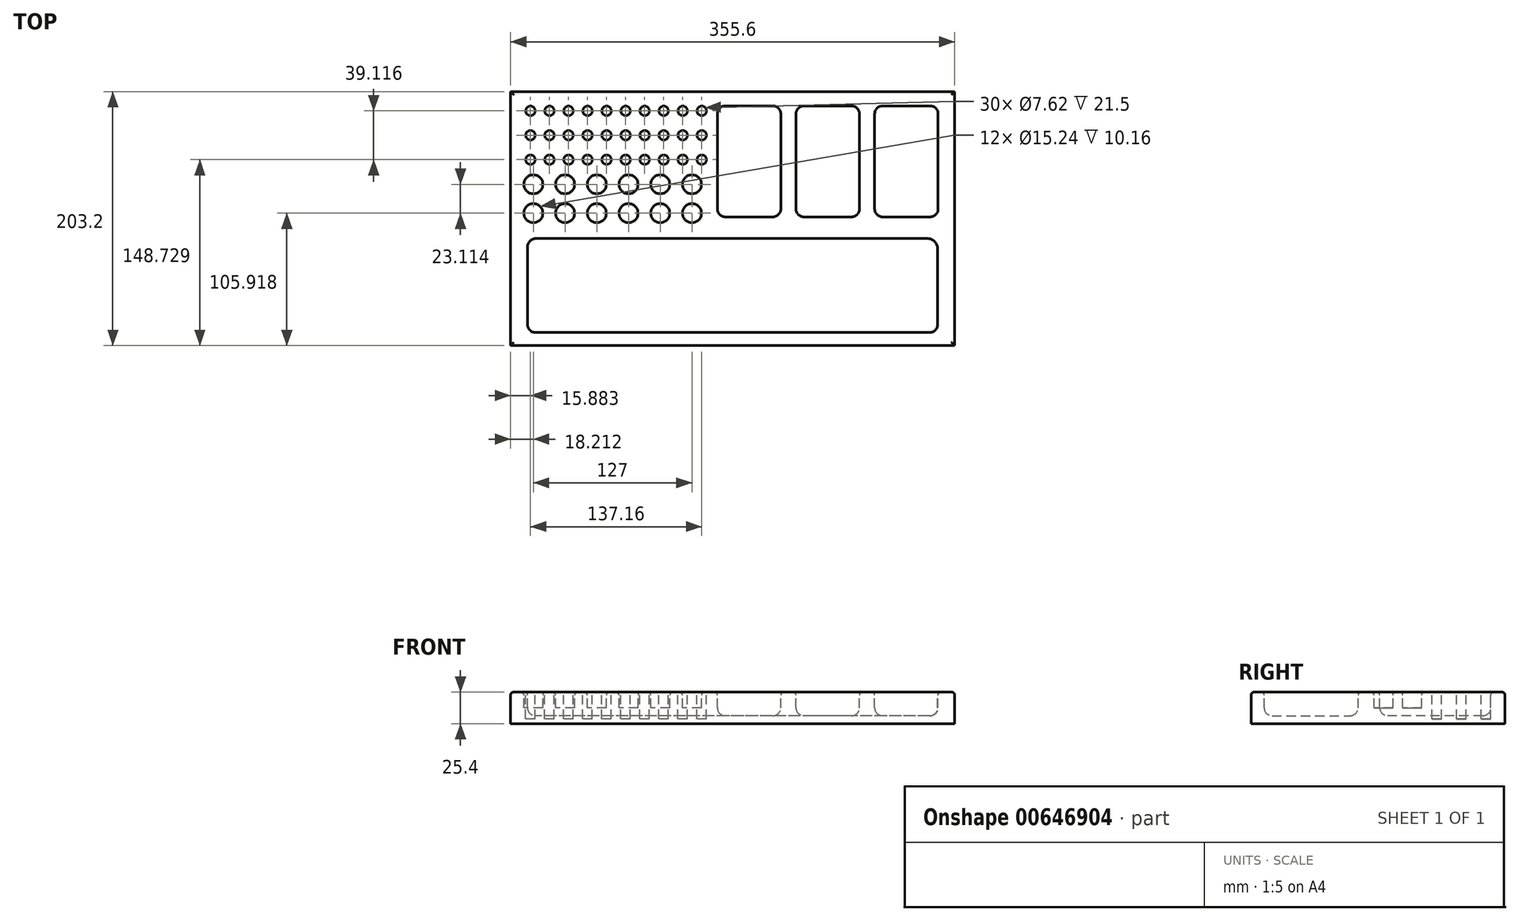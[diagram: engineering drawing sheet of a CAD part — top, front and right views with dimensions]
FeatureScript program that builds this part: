
annotation { "Feature Type Name" : "Feature", "Feature Type Description" : "" }
export const myFeature = defineFeature(function(context is Context, id is Id, definition is map)
    precondition{}
    {
        {
            var Q0;
            Q0=qCreatedBy(makeId("Top.planeOp"),FACE);
            var sketch = newSketch(context, id + "F0", { "sketchPlane" : qUnion([Q0])});
            skLineSegment(sketch, "E0.bottom", {"start": v(-59.89, 153) * mm, "end": v(295.71, 153) * mm});
            skLineSegment(sketch, "E0.top", {"start": v(-59.89, -50.2) * mm, "end": v(295.71, -50.2) * mm});
            skLineSegment(sketch, "E0.left", {"start": v(-59.89, 153) * mm, "end": v(-59.89, -50.2) * mm});
            skLineSegment(sketch, "E0.right", {"start": v(295.71, 153) * mm, "end": v(295.71, -50.2) * mm});
            skLineSegment(sketch, "E1", {"start": v(295.71, -6.07) * mm, "end": v(295.71, 49.4) * mm});
            skLineSegment(sketch, "E2.bottom", {"start": v(275.71, -39.83) * mm, "end": v(-39.97, -39.83) * mm});
            skLineSegment(sketch, "E2.top", {"start": v(273.64, 35.42) * mm, "end": v(-39.64, 35.42) * mm});
            skLineSegment(sketch, "E2.left", {"start": v(282.06, -33.48) * mm, "end": v(282.06, 27) * mm});
            skLineSegment(sketch, "E2.right", {"start": v(-46.32, -33.48) * mm, "end": v(-46.32, 28.74) * mm});
            skPoint(sketch, "E2.middle", {"position": v(117.87, -2.2) * mm});
            skCircle(sketch, "E3", {"center": v(-41.68, 78.82) * mm, "radius": 7.62 * mm});
            skCircle(sketch, "E4.0.1.0", {"center": v(-41.68, 55.7) * mm, "radius": 7.62 * mm});
            skCircle(sketch, "E4.1.0.0", {"center": v(-16.28, 78.82) * mm, "radius": 7.62 * mm});
            skCircle(sketch, "E4.1.1.0", {"center": v(-16.28, 55.7) * mm, "radius": 7.62 * mm});
            skCircle(sketch, "E4.2.0.0", {"center": v(9.12, 78.82) * mm, "radius": 7.62 * mm});
            skCircle(sketch, "E4.2.1.0", {"center": v(9.12, 55.7) * mm, "radius": 7.62 * mm});
            skCircle(sketch, "E4.3.0.0", {"center": v(34.52, 78.82) * mm, "radius": 7.62 * mm});
            skCircle(sketch, "E4.3.1.0", {"center": v(34.52, 55.7) * mm, "radius": 7.62 * mm});
            skLineSegment(sketch, "E4.direction1", {"start": v(-41.68, 78.82) * mm, "end": v(-16.28, 78.82) * mm, "construction": true});
            skLineSegment(sketch, "E4.direction2", {"start": v(-41.68, 78.82) * mm, "end": v(-41.68, 55.7) * mm, "construction": true});
            skCircle(sketch, "E5", {"center": v(-44, 137.63) * mm, "radius": 3.81 * mm});
            skCircle(sketch, "E6.0.1.0", {"center": v(-44, 118.08) * mm, "radius": 3.81 * mm});
            skCircle(sketch, "E6.0.2.0", {"center": v(-44, 98.52) * mm, "radius": 3.81 * mm});
            skCircle(sketch, "E6.1.0.0", {"center": v(-28.77, 137.63) * mm, "radius": 3.81 * mm});
            skCircle(sketch, "E6.1.1.0", {"center": v(-28.77, 118.08) * mm, "radius": 3.81 * mm});
            skCircle(sketch, "E6.1.2.0", {"center": v(-28.77, 98.52) * mm, "radius": 3.81 * mm});
            skCircle(sketch, "E6.2.0.0", {"center": v(-13.53, 137.63) * mm, "radius": 3.81 * mm});
            skCircle(sketch, "E6.2.1.0", {"center": v(-13.53, 118.08) * mm, "radius": 3.81 * mm});
            skCircle(sketch, "E6.2.2.0", {"center": v(-13.53, 98.52) * mm, "radius": 3.81 * mm});
            skCircle(sketch, "E6.3.0.0", {"center": v(1.71, 137.63) * mm, "radius": 3.81 * mm});
            skCircle(sketch, "E6.3.1.0", {"center": v(1.71, 118.08) * mm, "radius": 3.81 * mm});
            skCircle(sketch, "E6.3.2.0", {"center": v(1.71, 98.52) * mm, "radius": 3.81 * mm});
            skCircle(sketch, "E6.4.0.0", {"center": v(16.95, 137.63) * mm, "radius": 3.81 * mm});
            skCircle(sketch, "E6.4.1.0", {"center": v(16.95, 118.08) * mm, "radius": 3.81 * mm});
            skCircle(sketch, "E6.4.2.0", {"center": v(16.95, 98.52) * mm, "radius": 3.81 * mm});
            skCircle(sketch, "E6.5.0.0", {"center": v(32.2, 137.63) * mm, "radius": 3.81 * mm});
            skCircle(sketch, "E6.5.1.0", {"center": v(32.2, 118.08) * mm, "radius": 3.81 * mm});
            skCircle(sketch, "E6.5.2.0", {"center": v(32.2, 98.52) * mm, "radius": 3.81 * mm});
            skCircle(sketch, "E6.6.0.0", {"center": v(47.43, 137.63) * mm, "radius": 3.81 * mm});
            skCircle(sketch, "E6.6.1.0", {"center": v(47.43, 118.08) * mm, "radius": 3.81 * mm});
            skCircle(sketch, "E6.6.2.0", {"center": v(47.43, 98.52) * mm, "radius": 3.81 * mm});
            skCircle(sketch, "E6.7.0.0", {"center": v(62.67, 137.63) * mm, "radius": 3.81 * mm});
            skCircle(sketch, "E6.7.1.0", {"center": v(62.67, 118.08) * mm, "radius": 3.81 * mm});
            skCircle(sketch, "E6.7.2.0", {"center": v(62.67, 98.52) * mm, "radius": 3.81 * mm});
            skLineSegment(sketch, "E6.direction1", {"start": v(-44, 137.63) * mm, "end": v(-28.77, 137.63) * mm, "construction": true});
            skLineSegment(sketch, "E6.direction2", {"start": v(-44, 137.63) * mm, "end": v(-44, 118.08) * mm, "construction": true});
            skPoint(sketch, "E7.visualSharp", {"position": v(282.06, 35.42) * mm});
            skArc(sketch, "E7.filletArc", {"start": v(282.06, 27) * mm, "mid": v(279.6, 32.95) * mm, "end": v(273.64, 35.42) * mm});
            skPoint(sketch, "E8.visualSharp", {"position": v(282.06, -39.83) * mm});
            skArc(sketch, "E8.filletArc", {"start": v(275.71, -39.83) * mm, "mid": v(280.2, -37.97) * mm, "end": v(282.06, -33.48) * mm});
            skPoint(sketch, "E9.visualSharp", {"position": v(-46.32, -39.83) * mm});
            skArc(sketch, "E9.filletArc", {"start": v(-46.32, -33.48) * mm, "mid": v(-44.46, -37.97) * mm, "end": v(-39.97, -39.83) * mm});
            skPoint(sketch, "E10.visualSharp", {"position": v(-46.32, 35.42) * mm});
            skArc(sketch, "E10.filletArc", {"start": v(-39.64, 35.42) * mm, "mid": v(-44.36, 33.47) * mm, "end": v(-46.32, 28.74) * mm});
            skLineSegment(sketch, "E11.bottom", {"start": v(150.11, 141.61) * mm, "end": v(112.01, 141.61) * mm});
            skLineSegment(sketch, "E11.top", {"start": v(150.11, 52.71) * mm, "end": v(112.01, 52.71) * mm});
            skLineSegment(sketch, "E11.left", {"start": v(156.46, 135.26) * mm, "end": v(156.46, 59.06) * mm});
            skLineSegment(sketch, "E11.right", {"start": v(105.66, 135.26) * mm, "end": v(105.66, 59.06) * mm});
            skPoint(sketch, "E11.middle", {"position": v(131.06, 97.16) * mm});
            skPoint(sketch, "E12.visualSharp", {"position": v(105.66, 141.61) * mm});
            skArc(sketch, "E12.filletArc", {"start": v(112.01, 141.61) * mm, "mid": v(107.52, 139.75) * mm, "end": v(105.66, 135.26) * mm});
            skPoint(sketch, "E13.visualSharp", {"position": v(156.46, 141.61) * mm});
            skArc(sketch, "E13.filletArc", {"start": v(156.46, 135.26) * mm, "mid": v(154.6, 139.75) * mm, "end": v(150.11, 141.61) * mm});
            skPoint(sketch, "E14.visualSharp", {"position": v(156.46, 52.71) * mm});
            skArc(sketch, "E14.filletArc", {"start": v(150.11, 52.71) * mm, "mid": v(154.6, 54.57) * mm, "end": v(156.46, 59.06) * mm});
            skPoint(sketch, "E15.visualSharp", {"position": v(105.66, 52.71) * mm});
            skArc(sketch, "E15.filletArc", {"start": v(105.66, 59.06) * mm, "mid": v(107.52, 54.57) * mm, "end": v(112.01, 52.71) * mm});
            skPoint(sketch, "E16.1.0.0", {"position": v(194.05, 97.16) * mm});
            skPoint(sketch, "E16.1.0.1", {"position": v(219.45, 52.71) * mm});
            skPoint(sketch, "E16.1.0.2", {"position": v(168.65, 52.71) * mm});
            skLineSegment(sketch, "E16.1.0.3", {"start": v(219.45, 135.26) * mm, "end": v(219.45, 59.06) * mm});
            skLineSegment(sketch, "E16.1.0.4", {"start": v(213.1, 141.61) * mm, "end": v(175, 141.61) * mm});
            skPoint(sketch, "E16.1.0.5", {"position": v(219.45, 141.61) * mm});
            skLineSegment(sketch, "E16.1.0.6", {"start": v(213.1, 52.71) * mm, "end": v(175, 52.71) * mm});
            skPoint(sketch, "E16.1.0.7", {"position": v(168.65, 141.61) * mm});
            skLineSegment(sketch, "E16.1.0.8", {"start": v(168.65, 135.26) * mm, "end": v(168.65, 59.06) * mm});
            skArc(sketch, "E16.1.0.9", {"start": v(175, 141.61) * mm, "mid": v(170.51, 139.75) * mm, "end": v(168.65, 135.26) * mm});
            skArc(sketch, "E16.1.0.10", {"start": v(168.65, 59.06) * mm, "mid": v(170.51, 54.57) * mm, "end": v(175, 52.71) * mm});
            skArc(sketch, "E16.1.0.11", {"start": v(213.1, 52.71) * mm, "mid": v(217.6, 54.57) * mm, "end": v(219.45, 59.06) * mm});
            skArc(sketch, "E16.1.0.12", {"start": v(219.45, 135.26) * mm, "mid": v(217.6, 139.75) * mm, "end": v(213.1, 141.61) * mm});
            skLineSegment(sketch, "E16.direction1", {"start": v(131.06, 97.16) * mm, "end": v(194.05, 97.16) * mm, "construction": true});
            skPoint(sketch, "E17.0.2.0", {"position": v(257.04, 97.16) * mm});
            skPoint(sketch, "E17.1.2.0", {"position": v(282.44, 52.71) * mm});
            skPoint(sketch, "E17.2.2.0", {"position": v(231.64, 52.71) * mm});
            skLineSegment(sketch, "E17.3.2.0", {"start": v(282.44, 135.26) * mm, "end": v(282.44, 59.06) * mm});
            skLineSegment(sketch, "E17.6.2.0", {"start": v(276.1, 141.61) * mm, "end": v(238, 141.61) * mm});
            skPoint(sketch, "E17.9.2.0", {"position": v(282.44, 141.61) * mm});
            skLineSegment(sketch, "E17.10.2.0", {"start": v(276.1, 52.71) * mm, "end": v(238, 52.71) * mm});
            skPoint(sketch, "E17.13.2.0", {"position": v(231.64, 141.61) * mm});
            skLineSegment(sketch, "E17.14.2.0", {"start": v(231.64, 135.26) * mm, "end": v(231.64, 59.06) * mm});
            skArc(sketch, "E17.17.2.0", {"start": v(238, 141.61) * mm, "mid": v(233.5, 139.75) * mm, "end": v(231.64, 135.26) * mm});
            skArc(sketch, "E17.21.2.0", {"start": v(231.64, 59.06) * mm, "mid": v(233.5, 54.57) * mm, "end": v(238, 52.71) * mm});
            skArc(sketch, "E17.25.2.0", {"start": v(276.1, 52.71) * mm, "mid": v(280.58, 54.57) * mm, "end": v(282.44, 59.06) * mm});
            skArc(sketch, "E17.29.2.0", {"start": v(282.44, 135.26) * mm, "mid": v(280.58, 139.75) * mm, "end": v(276.1, 141.61) * mm});
            skCircle(sketch, "E18.0.4.0", {"center": v(59.92, 78.82) * mm, "radius": 7.62 * mm});
            skCircle(sketch, "E18.0.4.1", {"center": v(59.92, 55.7) * mm, "radius": 7.62 * mm});
            skCircle(sketch, "E19.0.8.0", {"center": v(77.91, 137.63) * mm, "radius": 3.81 * mm});
            skCircle(sketch, "E19.0.8.1", {"center": v(77.91, 118.08) * mm, "radius": 3.81 * mm});
            skCircle(sketch, "E19.0.8.2", {"center": v(77.91, 98.52) * mm, "radius": 3.81 * mm});
            skCircle(sketch, "E20.0.5.0", {"center": v(85.32, 78.82) * mm, "radius": 7.62 * mm});
            skCircle(sketch, "E20.0.5.1", {"center": v(85.32, 55.7) * mm, "radius": 7.62 * mm});
            skCircle(sketch, "E21.0.9.0", {"center": v(93.15, 137.63) * mm, "radius": 3.81 * mm});
            skCircle(sketch, "E21.0.9.1", {"center": v(93.15, 118.08) * mm, "radius": 3.81 * mm});
            skCircle(sketch, "E21.0.9.2", {"center": v(93.15, 98.52) * mm, "radius": 3.81 * mm});
            skSolve(sketch);
        }
        {
            var Q0;
            Q0=makeQuery(id+"F0.imprint","IMPRINT",FACE,{"disambiguationData":[TD([[makeQuery(id+"F0.imprint","IMPRINT",EDGE,{"derivedFrom":sQuery(id+"F0.wireOp",EDGE,"E6.4.2.0")}),1.0]])]});
            var Q1;
            Q1=makeQuery(id+"F0.imprint","IMPRINT",FACE,{"disambiguationData":[TD([[makeQuery(id+"F0.imprint","IMPRINT",EDGE,{"derivedFrom":sQuery(id+"F0.wireOp",EDGE,"E6.7.2.0")}),1.0]])]});
            var Q2;
            Q2=makeQuery(id+"F0.imprint","IMPRINT",FACE,{"disambiguationData":[TD([[makeQuery(id+"F0.imprint","IMPRINT",EDGE,{"derivedFrom":sQuery(id+"F0.wireOp",EDGE,"E6.2.1.0")}),1.0]])]});
            var Q3;
            Q3=makeQuery(id+"F0.imprint","IMPRINT",FACE,{"disambiguationData":[TD([[makeQuery(id+"F0.imprint","IMPRINT",EDGE,{"derivedFrom":sQuery(id+"F0.wireOp",EDGE,"E6.2.2.0")}),1.0]])]});
            var Q4;
            Q4=makeQuery(id+"F0.imprint","IMPRINT",FACE,{"disambiguationData":[TD([[makeQuery(id+"F0.imprint","IMPRINT",EDGE,{"derivedFrom":sQuery(id+"F0.wireOp",EDGE,"E6.5.2.0")}),1.0]])]});
            var Q5;
            Q5=makeQuery(id+"F0.imprint","IMPRINT",FACE,{"disambiguationData":[TD([[makeQuery(id+"F0.imprint","IMPRINT",EDGE,{"derivedFrom":sQuery(id+"F0.wireOp",EDGE,"E11.bottom")}),1.0]])]});
            var Q6;
            Q6=makeQuery(id+"F0.imprint","IMPRINT",FACE,{"disambiguationData":[TD([[makeQuery(id+"F0.imprint","IMPRINT",EDGE,{"derivedFrom":sQuery(id+"F0.wireOp",EDGE,"E6.4.1.0")}),1.0]])]});
            var Q7;
            Q7=makeQuery(id+"F0.imprint","IMPRINT",FACE,{"disambiguationData":[TD([[makeQuery(id+"F0.imprint","IMPRINT",EDGE,{"derivedFrom":sQuery(id+"F0.wireOp",EDGE,"E16.2.0.3")}),-1.0]])]});
            var Q8;
            Q8=makeQuery(id+"F0.imprint","IMPRINT",FACE,{"disambiguationData":[TD([[makeQuery(id+"F0.imprint","IMPRINT",EDGE,{"derivedFrom":sQuery(id+"F0.wireOp",EDGE,"E6.6.1.0")}),1.0]])]});
            var Q9;
            Q9=makeQuery(id+"F0.imprint","IMPRINT",FACE,{"disambiguationData":[TD([[makeQuery(id+"F0.imprint","IMPRINT",EDGE,{"derivedFrom":sQuery(id+"F0.wireOp",EDGE,"E6.0.2.0")}),1.0]])]});
            var Q10;
            Q10=makeQuery(id+"F0.imprint","IMPRINT",FACE,{"disambiguationData":[TD([[makeQuery(id+"F0.imprint","IMPRINT",EDGE,{"derivedFrom":sQuery(id+"F0.wireOp",EDGE,"E5")}),1.0]])]});
            var Q11;
            Q11=makeQuery(id+"F0.imprint","IMPRINT",FACE,{"disambiguationData":[TD([[makeQuery(id+"F0.imprint","IMPRINT",EDGE,{"derivedFrom":sQuery(id+"F0.wireOp",EDGE,"E6.0.1.0")}),1.0]])]});
            var Q12;
            Q12=makeQuery(id+"F0.imprint","IMPRINT",FACE,{"disambiguationData":[TD([[makeQuery(id+"F0.imprint","IMPRINT",EDGE,{"derivedFrom":sQuery(id+"F0.wireOp",EDGE,"E4.3.1.0")}),1.0]])]});
            var Q13;
            Q13=makeQuery(id+"F0.imprint","IMPRINT",FACE,{"disambiguationData":[TD([[makeQuery(id+"F0.imprint","IMPRINT",EDGE,{"derivedFrom":sQuery(id+"F0.wireOp",EDGE,"E4.2.1.0")}),1.0]])]});
            var Q14;
            Q14=makeQuery(id+"F0.imprint","IMPRINT",FACE,{"disambiguationData":[TD([[makeQuery(id+"F0.imprint","IMPRINT",EDGE,{"derivedFrom":sQuery(id+"F0.wireOp",EDGE,"9A4hbKAx-qqpV-GTlX-ATKJ-WJROtGpDy6VK.bottom")}),-1.0]])]});
            var Q15;
            Q15=makeQuery(id+"F0.imprint","IMPRINT",FACE,{"disambiguationData":[TD([[makeQuery(id+"F0.imprint","IMPRINT",EDGE,{"derivedFrom":sQuery(id+"F0.wireOp",EDGE,"E6.6.0.0")}),1.0]])]});
            var Q16;
            Q16=makeQuery(id+"F0.imprint","IMPRINT",FACE,{"disambiguationData":[TD([[makeQuery(id+"F0.imprint","IMPRINT",EDGE,{"derivedFrom":sQuery(id+"F0.wireOp",EDGE,"E6.7.0.0")}),1.0]])]});
            var Q17;
            Q17=makeQuery(id+"F0.imprint","IMPRINT",FACE,{"disambiguationData":[TD([[makeQuery(id+"F0.imprint","IMPRINT",EDGE,{"derivedFrom":sQuery(id+"F0.wireOp",EDGE,"E6.5.0.0")}),1.0]])]});
            var Q18;
            Q18=makeQuery(id+"F0.imprint","IMPRINT",FACE,{"disambiguationData":[TD([[makeQuery(id+"F0.imprint","IMPRINT",EDGE,{"derivedFrom":sQuery(id+"F0.wireOp",EDGE,"E4.3.0.0")}),1.0]])]});
            var Q19;
            Q19=makeQuery(id+"F0.imprint","IMPRINT",FACE,{"disambiguationData":[TD([[makeQuery(id+"F0.imprint","IMPRINT",EDGE,{"derivedFrom":sQuery(id+"F0.wireOp",EDGE,"E4.2.0.0")}),1.0]])]});
            var Q20;
            Q20=makeQuery(id+"F0.imprint","IMPRINT",FACE,{"disambiguationData":[TD([[makeQuery(id+"F0.imprint","IMPRINT",EDGE,{"derivedFrom":sQuery(id+"F0.wireOp",EDGE,"E4.1.1.0")}),1.0]])]});
            var Q21;
            Q21=makeQuery(id+"F0.imprint","IMPRINT",FACE,{"disambiguationData":[TD([[makeQuery(id+"F0.imprint","IMPRINT",EDGE,{"derivedFrom":sQuery(id+"F0.wireOp",EDGE,"E4.1.0.0")}),1.0]])]});
            var Q22;
            Q22=makeQuery(id+"F0.imprint","IMPRINT",FACE,{"disambiguationData":[TD([[makeQuery(id+"F0.imprint","IMPRINT",EDGE,{"derivedFrom":sQuery(id+"F0.wireOp",EDGE,"E4.0.1.0")}),1.0]])]});
            var Q23;
            Q23=makeQuery(id+"F0.imprint","IMPRINT",FACE,{"disambiguationData":[TD([[makeQuery(id+"F0.imprint","IMPRINT",EDGE,{"derivedFrom":sQuery(id+"F0.wireOp",EDGE,"E3")}),1.0]])]});
            var Q24;
            Q24=makeQuery(id+"F0.imprint","IMPRINT",FACE,{"disambiguationData":[TD([[makeQuery(id+"F0.imprint","IMPRINT",EDGE,{"derivedFrom":sQuery(id+"F0.wireOp",EDGE,"E6.6.2.0")}),1.0]])]});
            var Q25;
            Q25=makeQuery(id+"F0.imprint","IMPRINT",FACE,{"disambiguationData":[TD([[makeQuery(id+"F0.imprint","IMPRINT",EDGE,{"derivedFrom":sQuery(id+"F0.wireOp",EDGE,"E6.7.1.0")}),1.0]])]});
            var Q26;
            Q26=makeQuery(id+"F0.imprint","IMPRINT",FACE,{"disambiguationData":[TD([[makeQuery(id+"F0.imprint","IMPRINT",EDGE,{"derivedFrom":sQuery(id+"F0.wireOp",EDGE,"E2.bottom")}),-1.0]])]});
            var Q27;
            {var subQ3=sQuery(id+"F0.wireOp",EDGE,"E0.bottom");Q27=makeQuery(id+"F0.imprint","IMPRINT",FACE,{"disambiguationData":[TD([[makeQuery(id+"F0.imprint","IMPRINT",EDGE,{"derivedFrom":subQ3}),-1.0]])]});}
            var Q28;
            Q28=makeQuery(id+"F0.imprint","IMPRINT",FACE,{"disambiguationData":[TD([[makeQuery(id+"F0.imprint","IMPRINT",EDGE,{"derivedFrom":sQuery(id+"F0.wireOp",EDGE,"E6.3.1.0")}),1.0]])]});
            var Q29;
            Q29=makeQuery(id+"F0.imprint","IMPRINT",FACE,{"disambiguationData":[TD([[makeQuery(id+"F0.imprint","IMPRINT",EDGE,{"derivedFrom":sQuery(id+"F0.wireOp",EDGE,"E6.2.0.0")}),1.0]])]});
            var Q30;
            Q30=makeQuery(id+"F0.imprint","IMPRINT",FACE,{"disambiguationData":[TD([[makeQuery(id+"F0.imprint","IMPRINT",EDGE,{"derivedFrom":sQuery(id+"F0.wireOp",EDGE,"E6.1.1.0")}),1.0]])]});
            var Q31;
            Q31=makeQuery(id+"F0.imprint","IMPRINT",FACE,{"disambiguationData":[TD([[makeQuery(id+"F0.imprint","IMPRINT",EDGE,{"derivedFrom":sQuery(id+"F0.wireOp",EDGE,"E6.1.0.0")}),1.0]])]});
            var Q32;
            Q32=makeQuery(id+"F0.imprint","IMPRINT",FACE,{"disambiguationData":[TD([[makeQuery(id+"F0.imprint","IMPRINT",EDGE,{"derivedFrom":sQuery(id+"F0.wireOp",EDGE,"E6.5.1.0")}),1.0]])]});
            var Q33;
            Q33=makeQuery(id+"F0.imprint","IMPRINT",FACE,{"disambiguationData":[TD([[makeQuery(id+"F0.imprint","IMPRINT",EDGE,{"derivedFrom":sQuery(id+"F0.wireOp",EDGE,"E6.1.2.0")}),1.0]])]});
            var Q34;
            Q34=makeQuery(id+"F0.imprint","IMPRINT",FACE,{"disambiguationData":[TD([[makeQuery(id+"F0.imprint","IMPRINT",EDGE,{"derivedFrom":sQuery(id+"F0.wireOp",EDGE,"E6.4.0.0")}),1.0]])]});
            var Q35;
            Q35=makeQuery(id+"F0.imprint","IMPRINT",FACE,{"disambiguationData":[TD([[makeQuery(id+"F0.imprint","IMPRINT",EDGE,{"derivedFrom":sQuery(id+"F0.wireOp",EDGE,"E6.3.2.0")}),1.0]])]});
            var Q36;
            Q36=makeQuery(id+"F0.imprint","IMPRINT",FACE,{"disambiguationData":[TD([[makeQuery(id+"F0.imprint","IMPRINT",EDGE,{"derivedFrom":sQuery(id+"F0.wireOp",EDGE,"E16.1.0.3")}),-1.0]])]});
            var Q37;
            Q37=makeQuery(id+"F0.imprint","IMPRINT",FACE,{"disambiguationData":[TD([[makeQuery(id+"F0.imprint","IMPRINT",EDGE,{"derivedFrom":sQuery(id+"F0.wireOp",EDGE,"E6.3.0.0")}),1.0]])]});
            var Q38;
            Q38=makeQuery(id+"F0.imprint","IMPRINT",FACE,{"disambiguationData":[TD([[makeQuery(id+"F0.imprint","IMPRINT",EDGE,{"derivedFrom":sQuery(id+"F0.wireOp",EDGE,"E17.3.2.0")}),-1.0]])]});
            var Q39;
            Q39=makeQuery(id+"F0.imprint","IMPRINT",FACE,{"disambiguationData":[TD([[makeQuery(id+"F0.imprint","IMPRINT",EDGE,{"derivedFrom":sQuery(id+"F0.wireOp",EDGE,"E20.0.5.1")}),1.0]])]});
            var Q40;
            Q40=makeQuery(id+"F0.imprint","IMPRINT",FACE,{"disambiguationData":[TD([[makeQuery(id+"F0.imprint","IMPRINT",EDGE,{"derivedFrom":sQuery(id+"F0.wireOp",EDGE,"E18.0.4.1")}),1.0]])]});
            var Q41;
            Q41=makeQuery(id+"F0.imprint","IMPRINT",FACE,{"disambiguationData":[TD([[makeQuery(id+"F0.imprint","IMPRINT",EDGE,{"derivedFrom":sQuery(id+"F0.wireOp",EDGE,"E18.0.4.0")}),1.0]])]});
            var Q42;
            Q42=makeQuery(id+"F0.imprint","IMPRINT",FACE,{"disambiguationData":[TD([[makeQuery(id+"F0.imprint","IMPRINT",EDGE,{"derivedFrom":sQuery(id+"F0.wireOp",EDGE,"E20.0.5.0")}),1.0]])]});
            var Q43;
            Q43=makeQuery(id+"F0.imprint","IMPRINT",FACE,{"disambiguationData":[TD([[makeQuery(id+"F0.imprint","IMPRINT",EDGE,{"derivedFrom":sQuery(id+"F0.wireOp",EDGE,"E19.0.8.1")}),1.0]])]});
            var Q44;
            Q44=makeQuery(id+"F0.imprint","IMPRINT",FACE,{"disambiguationData":[TD([[makeQuery(id+"F0.imprint","IMPRINT",EDGE,{"derivedFrom":sQuery(id+"F0.wireOp",EDGE,"E21.0.9.1")}),1.0]])]});
            var Q45;
            Q45=makeQuery(id+"F0.imprint","IMPRINT",FACE,{"disambiguationData":[TD([[makeQuery(id+"F0.imprint","IMPRINT",EDGE,{"derivedFrom":sQuery(id+"F0.wireOp",EDGE,"E21.0.9.0")}),1.0]])]});
            var Q46;
            Q46=makeQuery(id+"F0.imprint","IMPRINT",FACE,{"disambiguationData":[TD([[makeQuery(id+"F0.imprint","IMPRINT",EDGE,{"derivedFrom":sQuery(id+"F0.wireOp",EDGE,"E19.0.8.0")}),1.0]])]});
            var Q47;
            Q47=makeQuery(id+"F0.imprint","IMPRINT",FACE,{"disambiguationData":[TD([[makeQuery(id+"F0.imprint","IMPRINT",EDGE,{"derivedFrom":sQuery(id+"F0.wireOp",EDGE,"E19.0.8.2")}),1.0]])]});
            var Q48;
            Q48=makeQuery(id+"F0.imprint","IMPRINT",FACE,{"disambiguationData":[TD([[makeQuery(id+"F0.imprint","IMPRINT",EDGE,{"derivedFrom":sQuery(id+"F0.wireOp",EDGE,"E21.0.9.2")}),1.0]])]});
            extrude(context, id + "F1", {"entities" : qUnion([Q0, Q1, Q2, Q3, Q4, Q5, Q6, Q7, Q8, Q9, Q10, Q11, Q12, Q13, Q14, Q15, Q16, Q17, Q18, Q19, Q20, Q21, Q22, Q23, Q24, Q25, Q26, Q27, Q28, Q29, Q30, Q31, Q32, Q33, Q34, Q35, Q36, Q37, Q38, Q39, Q40, Q41, Q42, Q43, Q44, Q45, Q46, Q47, Q48]), "depth" : -25.4 * mm, "offsetDistance" : 25.4 * mm});
        }
        {
            var Q0;
            Q0=makeQuery(id+"F0.imprint","IMPRINT",FACE,{"disambiguationData":[TD([[makeQuery(id+"F0.imprint","IMPRINT",EDGE,{"derivedFrom":sQuery(id+"F0.wireOp",EDGE,"9A4hbKAx-qqpV-GTlX-ATKJ-WJROtGpDy6VK.bottom")}),-1.0]])]});
            var Q1;
            Q1=makeQuery(id+"F0.imprint","IMPRINT",FACE,{"disambiguationData":[TD([[makeQuery(id+"F0.imprint","IMPRINT",EDGE,{"derivedFrom":sQuery(id+"F0.wireOp",EDGE,"E11.bottom")}),1.0]])]});
            var Q2;
            Q2=makeQuery(id+"F0.imprint","IMPRINT",FACE,{"disambiguationData":[TD([[makeQuery(id+"F0.imprint","IMPRINT",EDGE,{"derivedFrom":sQuery(id+"F0.wireOp",EDGE,"E16.1.0.3")}),-1.0]])]});
            var Q3;
            Q3=makeQuery(id+"F0.imprint","IMPRINT",FACE,{"disambiguationData":[TD([[makeQuery(id+"F0.imprint","IMPRINT",EDGE,{"derivedFrom":sQuery(id+"F0.wireOp",EDGE,"E16.2.0.3")}),-1.0]])]});
            var Q4;
            Q4=makeQuery(id+"F0.imprint","IMPRINT",FACE,{"disambiguationData":[TD([[makeQuery(id+"F0.imprint","IMPRINT",EDGE,{"derivedFrom":sQuery(id+"F0.wireOp",EDGE,"E2.bottom")}),-1.0]])]});
            var Q5;
            Q5=makeQuery(id+"F0.imprint","IMPRINT",FACE,{"disambiguationData":[TD([[makeQuery(id+"F0.imprint","IMPRINT",EDGE,{"derivedFrom":sQuery(id+"F0.wireOp",EDGE,"E17.3.2.0")}),-1.0]])]});
            extrude(context, id + "F2", {"entities" : qUnion([Q0, Q1, Q2, Q3, Q4, Q5]), "operationType" : NewBodyOperationType.REMOVE, "oppositeDirection" : true, "depth" : 19.05 * mm, "offsetDistance" : 25.4 * mm});
        }
        {
            var Q0;
            Q0=makeQuery(id+"F0.imprint","IMPRINT",FACE,{"disambiguationData":[TD([[makeQuery(id+"F0.imprint","IMPRINT",EDGE,{"derivedFrom":sQuery(id+"F0.wireOp",EDGE,"E3")}),1.0]])]});
            var Q1;
            Q1=makeQuery(id+"F0.imprint","IMPRINT",FACE,{"disambiguationData":[TD([[makeQuery(id+"F0.imprint","IMPRINT",EDGE,{"derivedFrom":sQuery(id+"F0.wireOp",EDGE,"E4.1.0.0")}),1.0]])]});
            var Q2;
            Q2=makeQuery(id+"F0.imprint","IMPRINT",FACE,{"disambiguationData":[TD([[makeQuery(id+"F0.imprint","IMPRINT",EDGE,{"derivedFrom":sQuery(id+"F0.wireOp",EDGE,"E4.2.0.0")}),1.0]])]});
            var Q3;
            Q3=makeQuery(id+"F0.imprint","IMPRINT",FACE,{"disambiguationData":[TD([[makeQuery(id+"F0.imprint","IMPRINT",EDGE,{"derivedFrom":sQuery(id+"F0.wireOp",EDGE,"E4.3.0.0")}),1.0]])]});
            var Q4;
            Q4=makeQuery(id+"F0.imprint","IMPRINT",FACE,{"disambiguationData":[TD([[makeQuery(id+"F0.imprint","IMPRINT",EDGE,{"derivedFrom":sQuery(id+"F0.wireOp",EDGE,"E4.3.1.0")}),1.0]])]});
            var Q5;
            Q5=makeQuery(id+"F0.imprint","IMPRINT",FACE,{"disambiguationData":[TD([[makeQuery(id+"F0.imprint","IMPRINT",EDGE,{"derivedFrom":sQuery(id+"F0.wireOp",EDGE,"E4.2.1.0")}),1.0]])]});
            var Q6;
            Q6=makeQuery(id+"F0.imprint","IMPRINT",FACE,{"disambiguationData":[TD([[makeQuery(id+"F0.imprint","IMPRINT",EDGE,{"derivedFrom":sQuery(id+"F0.wireOp",EDGE,"E4.1.1.0")}),1.0]])]});
            var Q7;
            Q7=makeQuery(id+"F0.imprint","IMPRINT",FACE,{"disambiguationData":[TD([[makeQuery(id+"F0.imprint","IMPRINT",EDGE,{"derivedFrom":sQuery(id+"F0.wireOp",EDGE,"E4.0.1.0")}),1.0]])]});
            var Q8;
            Q8=makeQuery(id+"F0.imprint","IMPRINT",FACE,{"disambiguationData":[TD([[makeQuery(id+"F0.imprint","IMPRINT",EDGE,{"derivedFrom":sQuery(id+"F0.wireOp",EDGE,"E18.0.4.0")}),1.0]])]});
            var Q9;
            Q9=makeQuery(id+"F0.imprint","IMPRINT",FACE,{"disambiguationData":[TD([[makeQuery(id+"F0.imprint","IMPRINT",EDGE,{"derivedFrom":sQuery(id+"F0.wireOp",EDGE,"E20.0.5.0")}),1.0]])]});
            var Q10;
            Q10=makeQuery(id+"F0.imprint","IMPRINT",FACE,{"disambiguationData":[TD([[makeQuery(id+"F0.imprint","IMPRINT",EDGE,{"derivedFrom":sQuery(id+"F0.wireOp",EDGE,"E18.0.4.1")}),1.0]])]});
            var Q11;
            Q11=makeQuery(id+"F0.imprint","IMPRINT",FACE,{"disambiguationData":[TD([[makeQuery(id+"F0.imprint","IMPRINT",EDGE,{"derivedFrom":sQuery(id+"F0.wireOp",EDGE,"E20.0.5.1")}),1.0]])]});
            extrude(context, id + "F3", {"entities" : qUnion([Q0, Q1, Q2, Q3, Q4, Q5, Q6, Q7, Q8, Q9, Q10, Q11]), "operationType" : NewBodyOperationType.REMOVE, "oppositeDirection" : true, "depth" : 12.7 * mm, "offsetDistance" : 25.4 * mm});
        }
        {
            var Q0;
            Q0=makeQuery(id+"F2.boolean.opBoolean","COPY",FACE,{"derivedFrom":makeQuery(id+"F2.opExtrude","CAP_FACE",FACE,{"disambiguationData":[OSD([sQuery(id+"F0.wireOp",EDGE,"E11.bottom"),sQuery(id+"F0.wireOp",EDGE,"E11.top"),sQuery(id+"F0.wireOp",EDGE,"E11.left"),sQuery(id+"F0.wireOp",EDGE,"E11.right"),sQuery(id+"F0.wireOp",EDGE,"E12.filletArc"),sQuery(id+"F0.wireOp",EDGE,"E13.filletArc"),sQuery(id+"F0.wireOp",EDGE,"E14.filletArc"),sQuery(id+"F0.wireOp",EDGE,"E15.filletArc")])],"isStart":false})});
            var Q1;
            Q1=makeQuery(id+"F2.boolean.opBoolean","COPY",FACE,{"derivedFrom":makeQuery(id+"F2.opExtrude","CAP_FACE",FACE,{"disambiguationData":[OSD([sQuery(id+"F0.wireOp",EDGE,"E16.1.0.3"),sQuery(id+"F0.wireOp",EDGE,"E16.1.0.4"),sQuery(id+"F0.wireOp",EDGE,"E16.1.0.6"),sQuery(id+"F0.wireOp",EDGE,"E16.1.0.8"),sQuery(id+"F0.wireOp",EDGE,"E16.1.0.9"),sQuery(id+"F0.wireOp",EDGE,"E16.1.0.10"),sQuery(id+"F0.wireOp",EDGE,"E16.1.0.11"),sQuery(id+"F0.wireOp",EDGE,"E16.1.0.12")])],"isStart":false})});
            var Q2;
            Q2=makeQuery(id+"F2.boolean.opBoolean","COPY",FACE,{"derivedFrom":makeQuery(id+"F2.opExtrude","CAP_FACE",FACE,{"disambiguationData":[OSD([sQuery(id+"F0.wireOp",EDGE,"E16.2.0.3"),sQuery(id+"F0.wireOp",EDGE,"E16.2.0.4"),sQuery(id+"F0.wireOp",EDGE,"E16.2.0.6"),sQuery(id+"F0.wireOp",EDGE,"E16.2.0.8"),sQuery(id+"F0.wireOp",EDGE,"E16.2.0.9"),sQuery(id+"F0.wireOp",EDGE,"E16.2.0.10"),sQuery(id+"F0.wireOp",EDGE,"E16.2.0.11"),sQuery(id+"F0.wireOp",EDGE,"E16.2.0.12")])],"isStart":false})});
            var Q3;
            Q3=makeQuery(id+"F2.boolean.opBoolean","COPY",FACE,{"derivedFrom":makeQuery(id+"F2.opExtrude","CAP_FACE",FACE,{"disambiguationData":[OSD([sQuery(id+"F0.wireOp",EDGE,"9A4hbKAx-qqpV-GTlX-ATKJ-WJROtGpDy6VK.bottom"),sQuery(id+"F0.wireOp",EDGE,"9A4hbKAx-qqpV-GTlX-ATKJ-WJROtGpDy6VK.top"),sQuery(id+"F0.wireOp",EDGE,"9A4hbKAx-qqpV-GTlX-ATKJ-WJROtGpDy6VK.left"),sQuery(id+"F0.wireOp",EDGE,"9A4hbKAx-qqpV-GTlX-ATKJ-WJROtGpDy6VK.right"),sQuery(id+"F0.wireOp",EDGE,"e477cadd-d493-4804-a7a2-170d6044e291.filletArc"),sQuery(id+"F0.wireOp",EDGE,"1fdbac66-44d3-491e-8bec-5f1541717a86.filletArc"),sQuery(id+"F0.wireOp",EDGE,"a5c90ecf-2896-4fb8-ad01-03dc71ea6826.filletArc"),sQuery(id+"F0.wireOp",EDGE,"4735ed0b-7448-4876-9ddf-5d306502fd43.filletArc")])],"isStart":false})});
            var Q4;
            Q4=makeQuery(id+"F2.boolean.opBoolean","COPY",FACE,{"derivedFrom":makeQuery(id+"F2.opExtrude","CAP_FACE",FACE,{"disambiguationData":[OSD([sQuery(id+"F0.wireOp",EDGE,"E2.bottom"),sQuery(id+"F0.wireOp",EDGE,"E2.top"),sQuery(id+"F0.wireOp",EDGE,"E2.left"),sQuery(id+"F0.wireOp",EDGE,"E2.right"),sQuery(id+"F0.wireOp",EDGE,"E7.filletArc"),sQuery(id+"F0.wireOp",EDGE,"E8.filletArc"),sQuery(id+"F0.wireOp",EDGE,"E9.filletArc"),sQuery(id+"F0.wireOp",EDGE,"E10.filletArc")])],"isStart":false})});
            var Q5;
            Q5=makeQuery(id+"F2.boolean.opBoolean","COPY",EDGE,{"derivedFrom":makeQuery(id+"F2.opExtrude","CAP_EDGE",EDGE,{"disambiguationData":[OSD([sQuery(id+"F0.wireOp",EDGE,"E17.6.2.0")])],"isStart":false})});
            fillet(context, id + "F4", {"entities" : qUnion([Q0, Q1, Q2, Q3, Q4, Q5]), "radius" : 6.35 * mm, "tangentPropagation" : true, "allowEdgeOverflow" : false});
        }
        {
            var Q0;
            Q0=makeQuery(id+"F1.opExtrude","CAP_FACE",FACE,{"disambiguationData":[OSD([sQuery(id+"F0.wireOp",EDGE,"E0.bottom"),sQuery(id+"F0.wireOp",EDGE,"E0.top"),sQuery(id+"F0.wireOp",EDGE,"E0.left"),sQuery(id+"F0.wireOp",EDGE,"E0.right"),sQuery(id+"F0.wireOp",EDGE,"E1")])],"isStart":true});
            fillet(context, id + "F5", {"entities" : qUnion([Q0]), "radius" : 2.54 * mm, "tangentPropagation" : true, "allowEdgeOverflow" : false});
        }
        {
            var Q0;
            Q0=makeQuery(id+"F0.imprint","IMPRINT",FACE,{"disambiguationData":[TD([[makeQuery(id+"F0.imprint","IMPRINT",EDGE,{"derivedFrom":sQuery(id+"F0.wireOp",EDGE,"E5")}),1.0]])]});
            var Q1;
            Q1=makeQuery(id+"F0.imprint","IMPRINT",FACE,{"disambiguationData":[TD([[makeQuery(id+"F0.imprint","IMPRINT",EDGE,{"derivedFrom":sQuery(id+"F0.wireOp",EDGE,"E6.0.1.0")}),1.0]])]});
            var Q2;
            Q2=makeQuery(id+"F0.imprint","IMPRINT",FACE,{"disambiguationData":[TD([[makeQuery(id+"F0.imprint","IMPRINT",EDGE,{"derivedFrom":sQuery(id+"F0.wireOp",EDGE,"E6.0.2.0")}),1.0]])]});
            var Q3;
            Q3=makeQuery(id+"F0.imprint","IMPRINT",FACE,{"disambiguationData":[TD([[makeQuery(id+"F0.imprint","IMPRINT",EDGE,{"derivedFrom":sQuery(id+"F0.wireOp",EDGE,"E6.1.2.0")}),1.0]])]});
            var Q4;
            Q4=makeQuery(id+"F0.imprint","IMPRINT",FACE,{"disambiguationData":[TD([[makeQuery(id+"F0.imprint","IMPRINT",EDGE,{"derivedFrom":sQuery(id+"F0.wireOp",EDGE,"E6.1.1.0")}),1.0]])]});
            var Q5;
            Q5=makeQuery(id+"F0.imprint","IMPRINT",FACE,{"disambiguationData":[TD([[makeQuery(id+"F0.imprint","IMPRINT",EDGE,{"derivedFrom":sQuery(id+"F0.wireOp",EDGE,"E6.2.1.0")}),1.0]])]});
            var Q6;
            Q6=makeQuery(id+"F0.imprint","IMPRINT",FACE,{"disambiguationData":[TD([[makeQuery(id+"F0.imprint","IMPRINT",EDGE,{"derivedFrom":sQuery(id+"F0.wireOp",EDGE,"E6.2.2.0")}),1.0]])]});
            var Q7;
            Q7=makeQuery(id+"F0.imprint","IMPRINT",FACE,{"disambiguationData":[TD([[makeQuery(id+"F0.imprint","IMPRINT",EDGE,{"derivedFrom":sQuery(id+"F0.wireOp",EDGE,"E6.3.2.0")}),1.0]])]});
            var Q8;
            Q8=makeQuery(id+"F0.imprint","IMPRINT",FACE,{"disambiguationData":[TD([[makeQuery(id+"F0.imprint","IMPRINT",EDGE,{"derivedFrom":sQuery(id+"F0.wireOp",EDGE,"E6.3.1.0")}),1.0]])]});
            var Q9;
            Q9=makeQuery(id+"F0.imprint","IMPRINT",FACE,{"disambiguationData":[TD([[makeQuery(id+"F0.imprint","IMPRINT",EDGE,{"derivedFrom":sQuery(id+"F0.wireOp",EDGE,"E6.4.1.0")}),1.0]])]});
            var Q10;
            Q10=makeQuery(id+"F0.imprint","IMPRINT",FACE,{"disambiguationData":[TD([[makeQuery(id+"F0.imprint","IMPRINT",EDGE,{"derivedFrom":sQuery(id+"F0.wireOp",EDGE,"E6.4.2.0")}),1.0]])]});
            var Q11;
            Q11=makeQuery(id+"F0.imprint","IMPRINT",FACE,{"disambiguationData":[TD([[makeQuery(id+"F0.imprint","IMPRINT",EDGE,{"derivedFrom":sQuery(id+"F0.wireOp",EDGE,"E6.5.1.0")}),1.0]])]});
            var Q12;
            Q12=makeQuery(id+"F0.imprint","IMPRINT",FACE,{"disambiguationData":[TD([[makeQuery(id+"F0.imprint","IMPRINT",EDGE,{"derivedFrom":sQuery(id+"F0.wireOp",EDGE,"E6.5.2.0")}),1.0]])]});
            var Q13;
            Q13=makeQuery(id+"F0.imprint","IMPRINT",FACE,{"disambiguationData":[TD([[makeQuery(id+"F0.imprint","IMPRINT",EDGE,{"derivedFrom":sQuery(id+"F0.wireOp",EDGE,"E6.1.0.0")}),1.0]])]});
            var Q14;
            Q14=makeQuery(id+"F0.imprint","IMPRINT",FACE,{"disambiguationData":[TD([[makeQuery(id+"F0.imprint","IMPRINT",EDGE,{"derivedFrom":sQuery(id+"F0.wireOp",EDGE,"E6.2.0.0")}),1.0]])]});
            var Q15;
            Q15=makeQuery(id+"F0.imprint","IMPRINT",FACE,{"disambiguationData":[TD([[makeQuery(id+"F0.imprint","IMPRINT",EDGE,{"derivedFrom":sQuery(id+"F0.wireOp",EDGE,"E6.3.0.0")}),1.0]])]});
            var Q16;
            Q16=makeQuery(id+"F0.imprint","IMPRINT",FACE,{"disambiguationData":[TD([[makeQuery(id+"F0.imprint","IMPRINT",EDGE,{"derivedFrom":sQuery(id+"F0.wireOp",EDGE,"E6.4.0.0")}),1.0]])]});
            var Q17;
            Q17=makeQuery(id+"F0.imprint","IMPRINT",FACE,{"disambiguationData":[TD([[makeQuery(id+"F0.imprint","IMPRINT",EDGE,{"derivedFrom":sQuery(id+"F0.wireOp",EDGE,"E6.5.0.0")}),1.0]])]});
            var Q18;
            Q18=makeQuery(id+"F0.imprint","IMPRINT",FACE,{"disambiguationData":[TD([[makeQuery(id+"F0.imprint","IMPRINT",EDGE,{"derivedFrom":sQuery(id+"F0.wireOp",EDGE,"E6.6.0.0")}),1.0]])]});
            var Q19;
            Q19=makeQuery(id+"F0.imprint","IMPRINT",FACE,{"disambiguationData":[TD([[makeQuery(id+"F0.imprint","IMPRINT",EDGE,{"derivedFrom":sQuery(id+"F0.wireOp",EDGE,"E6.7.0.0")}),1.0]])]});
            var Q20;
            Q20=makeQuery(id+"F0.imprint","IMPRINT",FACE,{"disambiguationData":[TD([[makeQuery(id+"F0.imprint","IMPRINT",EDGE,{"derivedFrom":sQuery(id+"F0.wireOp",EDGE,"E6.6.1.0")}),1.0]])]});
            var Q21;
            Q21=makeQuery(id+"F0.imprint","IMPRINT",FACE,{"disambiguationData":[TD([[makeQuery(id+"F0.imprint","IMPRINT",EDGE,{"derivedFrom":sQuery(id+"F0.wireOp",EDGE,"E6.7.1.0")}),1.0]])]});
            var Q22;
            Q22=makeQuery(id+"F0.imprint","IMPRINT",FACE,{"disambiguationData":[TD([[makeQuery(id+"F0.imprint","IMPRINT",EDGE,{"derivedFrom":sQuery(id+"F0.wireOp",EDGE,"E6.6.2.0")}),1.0]])]});
            var Q23;
            Q23=makeQuery(id+"F0.imprint","IMPRINT",FACE,{"disambiguationData":[TD([[makeQuery(id+"F0.imprint","IMPRINT",EDGE,{"derivedFrom":sQuery(id+"F0.wireOp",EDGE,"E6.7.2.0")}),1.0]])]});
            var Q24;
            Q24=makeQuery(id+"F0.imprint","IMPRINT",FACE,{"disambiguationData":[TD([[makeQuery(id+"F0.imprint","IMPRINT",EDGE,{"derivedFrom":sQuery(id+"F0.wireOp",EDGE,"E19.0.8.2")}),1.0]])]});
            var Q25;
            Q25=makeQuery(id+"F0.imprint","IMPRINT",FACE,{"disambiguationData":[TD([[makeQuery(id+"F0.imprint","IMPRINT",EDGE,{"derivedFrom":sQuery(id+"F0.wireOp",EDGE,"E19.0.8.1")}),1.0]])]});
            var Q26;
            Q26=makeQuery(id+"F0.imprint","IMPRINT",FACE,{"disambiguationData":[TD([[makeQuery(id+"F0.imprint","IMPRINT",EDGE,{"derivedFrom":sQuery(id+"F0.wireOp",EDGE,"E19.0.8.0")}),1.0]])]});
            var Q27;
            Q27=makeQuery(id+"F0.imprint","IMPRINT",FACE,{"disambiguationData":[TD([[makeQuery(id+"F0.imprint","IMPRINT",EDGE,{"derivedFrom":sQuery(id+"F0.wireOp",EDGE,"E21.0.9.0")}),1.0]])]});
            var Q28;
            Q28=makeQuery(id+"F0.imprint","IMPRINT",FACE,{"disambiguationData":[TD([[makeQuery(id+"F0.imprint","IMPRINT",EDGE,{"derivedFrom":sQuery(id+"F0.wireOp",EDGE,"E21.0.9.1")}),1.0]])]});
            var Q29;
            Q29=makeQuery(id+"F0.imprint","IMPRINT",FACE,{"disambiguationData":[TD([[makeQuery(id+"F0.imprint","IMPRINT",EDGE,{"derivedFrom":sQuery(id+"F0.wireOp",EDGE,"E21.0.9.2")}),1.0]])]});
            extrude(context, id + "F6", {"entities" : qUnion([Q0, Q1, Q2, Q3, Q4, Q5, Q6, Q7, Q8, Q9, Q10, Q11, Q12, Q13, Q14, Q15, Q16, Q17, Q18, Q19, Q20, Q21, Q22, Q23, Q24, Q25, Q26, Q27, Q28, Q29]), "operationType" : NewBodyOperationType.REMOVE, "oppositeDirection" : true, "depth" : 21.5 * mm, "offsetDistance" : 25 * mm});
        }
    });
